# Revit family: ACO ALU Cover 1
name_source: partatom
category: Generic Models
revit_build: Autodesk Revit 2014 (Build: 20130308_1515(x64)
units: mm (PartAtom-declared; Revit-internal decimal feet)

## types (18) — shared parameters
Body Material = Aluminium
Body Recyclable = Fully recyclable
Body Recycled material content = Approx 90%
Fax = +44 (0)1462 851490
Grate Type = Recessed Aluminium Access Cover
Installation guidelines = http://issuu.com
Maintenance guidelines = http://issuu.com
Manufacturer = ACO Building Drainage
NBS Specification = http://issuu.com
Overall Height = 73 mm  [stored 0.239501 ft]
Price = POA - contact ACO
Product Description = ACO Alucover
Product Range = ACO Alucover
Product Standard = Fabricated Access Covers Trade Association (FACTA)
Product Type = Recessed Aluminium Access Cover
Telephone = +44 (0)1462 816666
Website = www.acobd.com

## per-type parameters (varying)
| type | Approx Cover Weight (Fully Filled) Kg | Clear Length | Clear Opening | Clear Width | FACTA Load Class (50mm Concrete Infill) | FACTA Load Class (70mm Concrete Infill) | Overall Length | Overall Size (W x L x H) | Overall Width | Product Code | Unfilled Weight (kg) |
| 405340 - ACO ALU Cover - 300 x 300 | 13 | 300 mm  [stored 0.984252 ft] | 300 x 300 | 300 mm  [stored 0.984252 ft] | AAA | B | 398 mm  [stored 1.30577 ft] | 398 x 398 x 73 | 398 mm  [stored 1.30577 ft] | 405340 | 4.0 |
| 405341 - ACO ALU Cover - 400 x 400 | 23 | 400 mm  [stored 1.31234 ft] | 400 x 400 | 400 mm  [stored 1.31234 ft] | AAA | B | 498 mm  [stored 1.63386 ft] | 498 x 498 x 73 | 498 mm  [stored 1.63386 ft] | 405341 | 5.0 |
| 405342 - ACO ALU Cover - 450 x 450 | 29 | 450 mm  [stored 1.47638 ft] | 450 x 450 | 450 mm  [stored 1.47638 ft] | AA | B | 548 mm  [stored 1.7979 ft] | 548 x 548 x73 | 548 mm  [stored 1.7979 ft] | 405342 | 6.0 |
| 405343 - ACO ALU Cover - 500 x 500 | 36 | 500 mm  [stored 1.64042 ft] | 500 x 500 | 500 mm  [stored 1.64042 ft] | AA | B | 598 mm  [stored 1.96194 ft] | 598 x 598 x 73 | 598 mm  [stored 1.96194 ft] | 405343 | 7.0 |
| 405344 - ACO ALU Cover - 600 x 400 | 35 | 400 mm  [stored 1.31234 ft] | 600 x 400 | 600 mm | AAA | B | 498 mm  [stored 1.63386 ft] | 698 x 498 x 73 | 698 mm  [stored 2.29003 ft] | 405344 | 7.0 |
| 406622 - ACO ALU Cover - 600 x 450 | 39 | 450 mm  [stored 1.47638 ft] | 600 x 450 | 600 mm | AA | B | 548 mm  [stored 1.7979 ft] | 698 x 548 x 73 | 698 mm  [stored 2.29003 ft] | 406622 | 7.0 |
| 405345 - ACO ALU Cover - 600 x 600 | 53 | 600 mm | 600 x 600 | 600 mm | AA | B | 698 mm  [stored 2.29003 ft] | 698 x 698 x73 | 698 mm  [stored 2.29003 ft] | 405345 | 8.0 |
| 406624 - ACO ALU Cover - 675 x 675 | 64 | 675 mm  [stored 2.21457 ft] | 675 x 675 | 675 mm  [stored 2.21457 ft] | A | AAA | 773 mm  [stored 2.53609 ft] | 773 x 773 x73 | 773 mm  [stored 2.53609 ft] | 406624 | 10.0 |
| 405346 - ACO ALU Cover - 800 x 600 | 71 | 600 mm | 800 x 600 | 800 mm  [stored 2.62467 ft] | AA | B | 698 mm  [stored 2.29003 ft] | 898 x 698 x 73 | 898 mm  [stored 2.94619 ft] | 405346 | 10.0 |
| 405347 - ACO ALU Cover - 700 x 700 | 73 | 700 mm  [stored 2.29659 ft] | 700 x 700 | 700 mm  [stored 2.29659 ft] | A | AAA | 798 mm  [stored 2.61811 ft] | 798 x 798 x73 | 798 mm  [stored 2.61811 ft] | 405347 | 10.0 |
| 406623 - ACO ALU Cover - 750 x 600 | 66 | 600 mm | 750 x 600 | 750 mm  [stored 2.46063 ft] | AA | B | 698 mm  [stored 2.29003 ft] | 848 x 698 x73 | 848 mm  [stored 2.78215 ft] | 406623 | 10.0 |
| 406625 - ACO ALU Cover - 750 x 750 | 83 | 750 mm  [stored 2.46063 ft] | 750 x750 | 750 mm  [stored 2.46063 ft] | A | AAA | 848 mm  [stored 2.78215 ft] | 848 x 848 x73 | 848 mm  [stored 2.78215 ft] | 406625
406625 | 11.0 |
| 405348 - ACO ALU Cover - 800 x 800 | 95 | 800 mm  [stored 2.62467 ft] | 800 x 800 | 800 mm  [stored 2.62467 ft] | A | AAA | 898 mm  [stored 2.94619 ft] | 898 x 898 x 73 | 898 mm  [stored 2.94619 ft] | 405348 | 12.0 |
| 406626 - ACO ALU Cover - 900 x 600 | 80 | 600 mm | 900 x 600 | 900 mm  [stored 2.95276 ft] | AA | B | 698 mm  [stored 2.29003 ft] | 998 x 698 x 73 | 998 mm  [stored 3.27428 ft] | 406626 | 11.0 |
| 406627 - ACO ALU Cover - 900 x 900 | 120 | 900 mm  [stored 2.95276 ft] | 900 x 900 | 900 mm  [stored 2.95276 ft] | A | AA | 998 mm  [stored 3.27428 ft] | 998 x 998 x 73 | 998 mm  [stored 3.27428 ft] | 406627 | 14.0 |
| 405826 - ACO ALU Cover - 1000 x 600 | 89 | 600 mm | 1000 x 600 | 1000 mm  [stored 3.28084 ft] | AA | B | 698 mm  [stored 2.29003 ft] | 1098 x 698 x 73 | 1098 mm  [stored 3.60236 ft] | 405826 | 12.0 |
| 405349 - ACO ALU Cover - 1000 x 800 | 120 | 800 mm  [stored 2.62467 ft] | 1000 x 800 | 1000 mm  [stored 3.28084 ft] | AA | AAA | 898 mm  [stored 2.94619 ft] | 1098 x 898 x 73 | 1098 mm  [stored 3.60236 ft] | 405349 | 13.0 |
| 405350 - ACO ALU Cover - 1000 x 1000 | 150 | 1000 mm  [stored 3.28084 ft] | 1000 x 1000 | 1000 mm  [stored 3.28084 ft] | A | AA | 1098 mm  [stored 3.60236 ft] | 1098 x 1098 x 73 | 1098 mm  [stored 3.60236 ft] | 405350 | 16.0 |

note: [stored X ft] marks values corroborated as IEEE doubles in the binary element streams (Revit-internal decimal feet)

## geometry (parser evidence)
native form markers: Extrusion x1, Sweep x2
no freeform markers — native parametric forms only
